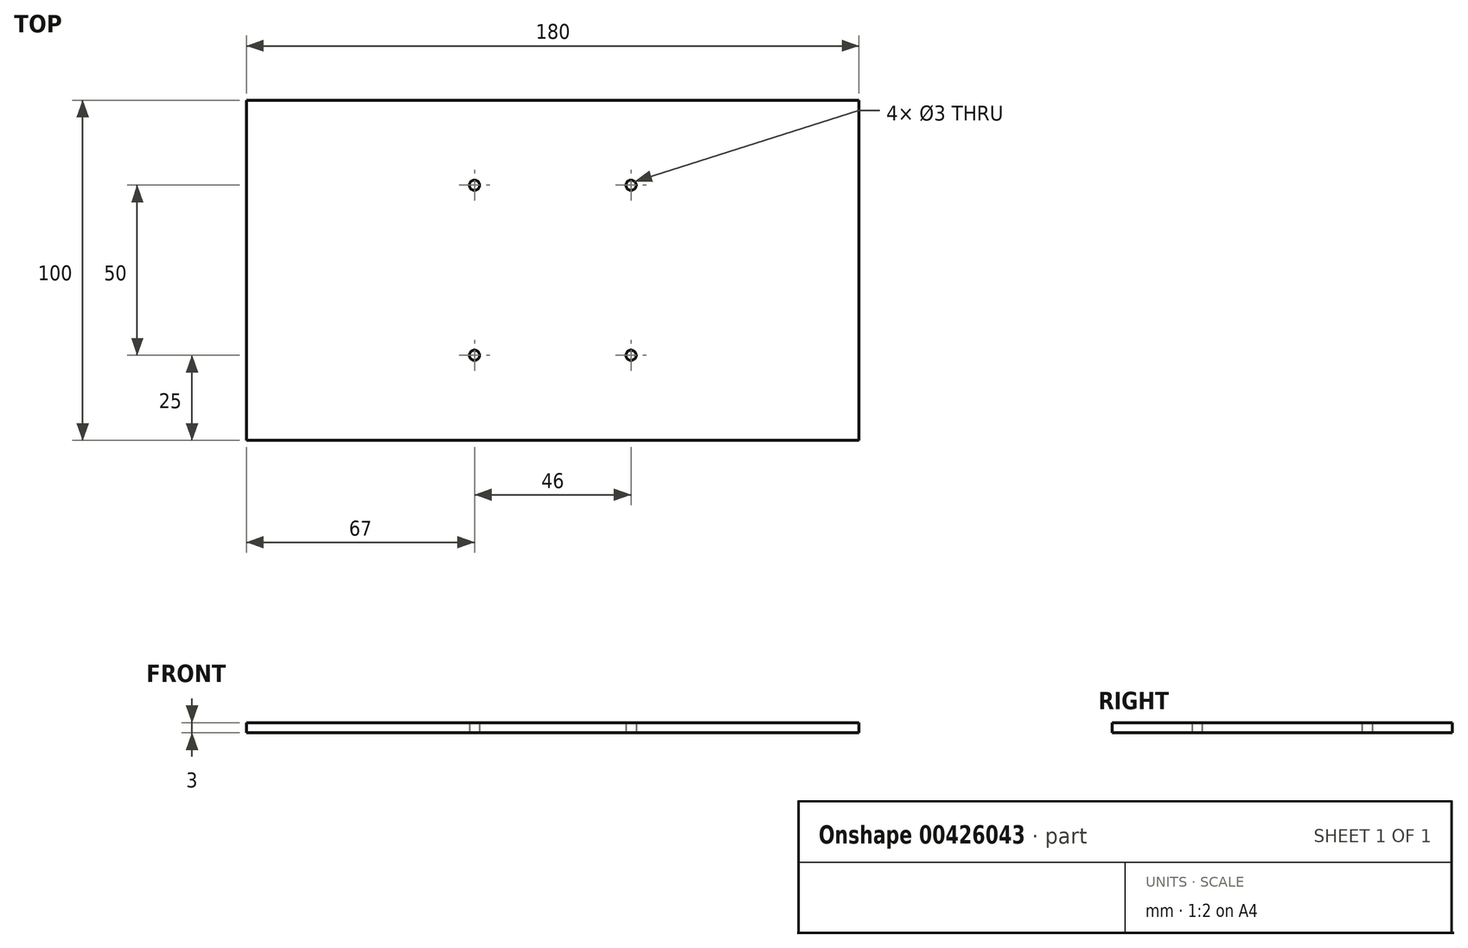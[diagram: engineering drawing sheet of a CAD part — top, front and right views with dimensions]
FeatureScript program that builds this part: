
annotation { "Feature Type Name" : "Feature", "Feature Type Description" : "" }
export const myFeature = defineFeature(function(context is Context, id is Id, definition is map)
    precondition{}
    {
        {
            var Q0;
            Q0=qCreatedBy(makeId("Top.planeOp"),FACE);
            var sketch = newSketch(context, id + "F0", { "sketchPlane" : qUnion([Q0])});
            skLineSegment(sketch, "E0.bottom", {"start": v(90, -50) * mm, "end": v(-90, -50) * mm});
            skLineSegment(sketch, "E0.top", {"start": v(90, 50) * mm, "end": v(-90, 50) * mm});
            skLineSegment(sketch, "E0.left", {"start": v(90, -50) * mm, "end": v(90, 50) * mm});
            skLineSegment(sketch, "E0.right", {"start": v(-90, -50) * mm, "end": v(-90, 50) * mm});
            skPoint(sketch, "E0.middle", {"position": v(0, 0) * mm});
            skCircle(sketch, "E1", {"center": v(-23, 25) * mm, "radius": 1.5 * mm});
            skCircle(sketch, "E2.MirrorC", {"center": v(23, 25) * mm, "radius": 1.5 * mm});
            skCircle(sketch, "E3.MirrorC", {"center": v(-23, -25) * mm, "radius": 1.5 * mm});
            skCircle(sketch, "E4.MirrorC", {"center": v(23, -25) * mm, "radius": 1.5 * mm});
            skSolve(sketch);
        }
        {
            var Q0;
            Q0=makeQuery(id+"F0.imprint","IMPRINT",FACE,{"disambiguationData":[TD([[makeQuery(id+"F0.imprint","IMPRINT",EDGE,{"derivedFrom":sQuery(id+"F0.wireOp",EDGE,"E0.bottom")}),-1.0]])]});
            extrude(context, id + "F1", {"entities" : qUnion([Q0]), "depth" : 3 * mm});
        }
    });
